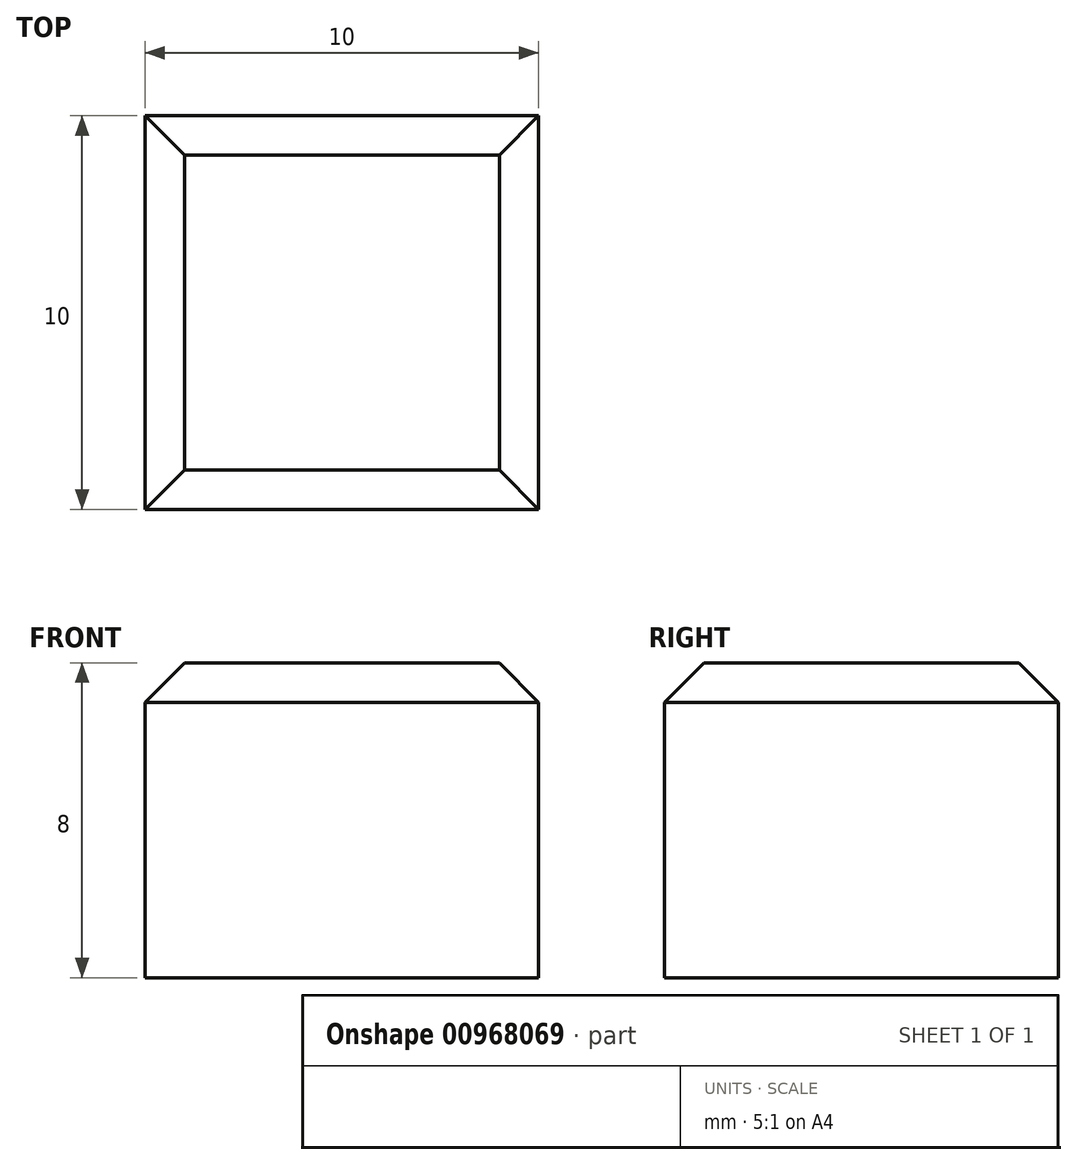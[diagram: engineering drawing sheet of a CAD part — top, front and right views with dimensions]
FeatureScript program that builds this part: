
annotation { "Feature Type Name" : "Feature", "Feature Type Description" : "" }
export const myFeature = defineFeature(function(context is Context, id is Id, definition is map)
    precondition{}
    {
        {
            var Q0;
            Q0=qCreatedBy(makeId("Top.planeOp"),FACE);
            var sketch = newSketch(context, id + "F0", { "sketchPlane" : qUnion([Q0])});
            skLineSegment(sketch, "E0.bottom", {"start": v(-42.43, 10) * mm, "end": v(-32.43, 10) * mm});
            skLineSegment(sketch, "E0.top", {"start": v(-42.43, 0) * mm, "end": v(-32.43, 0) * mm});
            skLineSegment(sketch, "E0.left", {"start": v(-42.43, 10) * mm, "end": v(-42.43, 0) * mm});
            skLineSegment(sketch, "E0.right", {"start": v(-32.43, 10) * mm, "end": v(-32.43, 0) * mm});
            skSolve(sketch);
        }
        {
            var Q0;
            Q0=makeQuery(id+"F0.imprint","IMPRINT",FACE,{"disambiguationData":[TD([[makeQuery(id+"F0.imprint","IMPRINT",EDGE,{"derivedFrom":sQuery(id+"F0.wireOp",EDGE,"E0.bottom")}),-1.0]])]});
            extrude(context, id + "F1", {"entities" : qUnion([Q0]), "depth" : 8 * mm, "offsetDistance" : 25 * mm});
        }
        {
            var Q0;
            Q0=makeQuery(id+"F1.opExtrude","CAP_EDGE",EDGE,{"disambiguationData":[OSD([sQuery(id+"F0.wireOp",EDGE,"E0.right")])],"isStart":false});
            var Q1;
            Q1=makeQuery(id+"F1.opExtrude","CAP_EDGE",EDGE,{"disambiguationData":[OSD([sQuery(id+"F0.wireOp",EDGE,"E0.top")])],"isStart":false});
            var Q2;
            Q2=makeQuery(id+"F1.opExtrude","CAP_EDGE",EDGE,{"disambiguationData":[OSD([sQuery(id+"F0.wireOp",EDGE,"E0.left")])],"isStart":false});
            var Q3;
            Q3=makeQuery(id+"F1.opExtrude","CAP_EDGE",EDGE,{"disambiguationData":[OSD([sQuery(id+"F0.wireOp",EDGE,"E0.bottom")])],"isStart":false});
            chamfer(context, id + "F2", {"entities" : qUnion([Q0, Q1, Q2, Q3]), "width" : 1 * mm, "tangentPropagation" : true});
        }
    });
